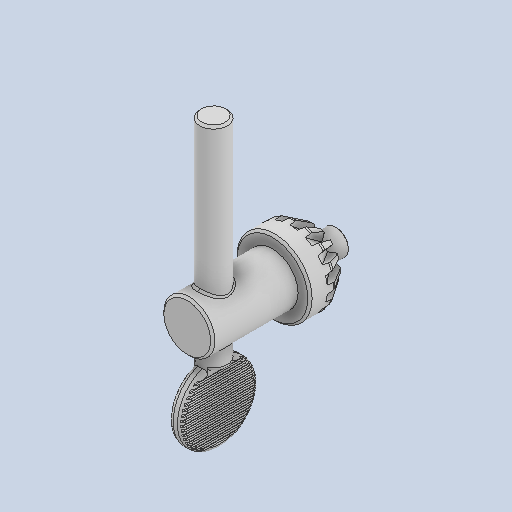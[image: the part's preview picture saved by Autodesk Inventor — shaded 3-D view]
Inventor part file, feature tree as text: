
AUTODESK INVENTOR PART (.ipt)
format: ipt  version: 2024 (Build 280153000, 153)  size: 718,336 bytes
history: native  units: in
note: dims shown in document units (in); Inventor stores cm internally (conversion verified against a paired STEP export)
features: chamfer x1
ambient origin geometry x8: Origin, YZ Plane, XZ Plane, XY Plane, X Axis, Y Axis, Z Axis, Center Point
bodies: Solid1 (feature_tree)
feature tree (1):
  chamfer  "Chamfer5"  [1 undecoded]
note: 1 required parameter value undecoded (feature->parameter linkage not recoverable at this tier; creation-order binding heuristic only, values carry confidence <= 0.55)
